# Revit family: Haworth_Zody_Chair_Guest
name_source: partatom
category: Furniture
revit_build: Autodesk Revit 2018 (Build: 20170223_1515(x64)
units: mm (PartAtom-declared; Revit-internal decimal feet)

## family parameters
Always vertical = Yes
Cut with Voids When Loaded = No
OmniClass Number = 23.40.70.14.64.11
OmniClass Title = Office Furniture
Room Calculation Point = No
Shared = No
Work Plane-Based = No

## types (2) — shared parameters
Arm Cap Finish = Haworth _ Polymer _ Black
Assembly Code = E2020200
Back Finish = Haworth _ Fabric _ Zinger _ Gravel NI-4
Base Finish = Haworth _ Metal _ Polished Aluminum
Depth = 22 "
Description = Haworth - Chair - Zody Guest
Fabric Back = Yes
Manufacturer = Haworth
Model = SZG
Revision Number = 3
Seat Finish = Haworth _ Fabric _ Zinger _ Gravel NI-4
Solid Back = No
Sustainability Info = http://media.haworth.com
URL = www.haworth.com
URL - Product = https://www.haworth.com
Warranty = http://www.haworth.com
Width = 22 "

## per-type parameters (varying)
| type | Legs | Sled |
| 4 Leg Base | Yes | No |
| Sled Base | No | Yes |

## geometry (parser evidence)
native form markers: Sweep x3
no freeform markers — native parametric forms only
